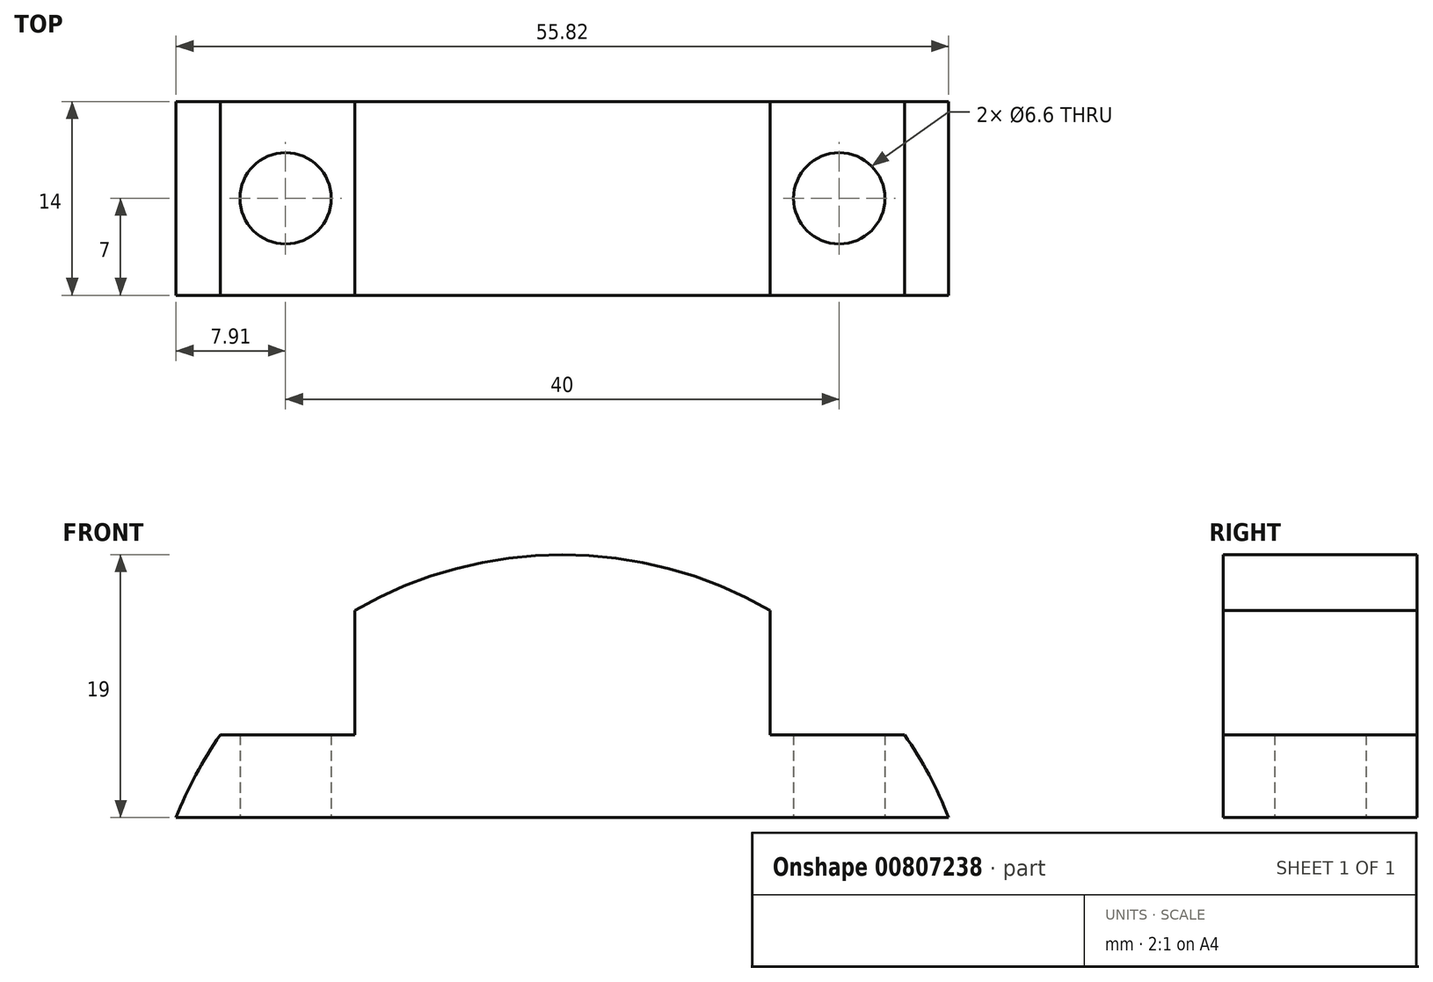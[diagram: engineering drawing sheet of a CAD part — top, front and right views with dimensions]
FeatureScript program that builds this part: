
annotation { "Feature Type Name" : "Feature", "Feature Type Description" : "" }
export const myFeature = defineFeature(function(context is Context, id is Id, definition is map)
    precondition{}
    {
        {
            var Q0;
            Q0=qCreatedBy(makeId("Front.planeOp"),FACE);
            var sketch = newSketch(context, id + "F0", { "sketchPlane" : qUnion([Q0])});
            skArc(sketch, "E0", {"start": v(27.91, 11) * mm, "mid": v(26.48, 14.1) * mm, "end": v(24.72, 17) * mm});
            skLineSegment(sketch, "E1", {"start": v(-27.91, 11) * mm, "end": v(27.91, 11) * mm});
            skLineSegment(sketch, "E2", {"start": v(0, 0) * mm, "end": v(0, -11.85) * mm, "construction": true});
            skLineSegment(sketch, "E3", {"start": v(-24.72, 17) * mm, "end": v(-15, 17) * mm});
            skLineSegment(sketch, "E4", {"start": v(15, 17) * mm, "end": v(15, 25.98) * mm});
            skLineSegment(sketch, "E5.MirrorCS", {"start": v(-15, 17) * mm, "end": v(-15, 25.98) * mm});
            skArc(sketch, "E6.trimOffspring", {"start": v(15, 25.98) * mm, "mid": v(0, 30) * mm, "end": v(-15, 25.98) * mm});
            skArc(sketch, "E7.trimOffspring", {"start": v(-24.72, 17) * mm, "mid": v(-26.48, 14.1) * mm, "end": v(-27.91, 11) * mm});
            skLineSegment(sketch, "E8.trimOffspring", {"start": v(15, 17) * mm, "end": v(24.72, 17) * mm});
            skSolve(sketch);
        }
        {
            var Q0;
            Q0 = qSketchRegion(id + "F0", true);
            extrude(context, id + "F1", {"entities" : qUnion([Q0]), "depth" : 14 * mm, "offsetDistance" : 25 * mm, "symmetric" : true});
        }
        {
            var Q0;
            Q0=makeQuery(id+"F1.opExtrude","SWEPT_FACE",FACE,{"disambiguationData":[OSD([sQuery(id+"F0.wireOp",EDGE,"E1")])]});
            var sketch = newSketch(context, id + "F2", { "sketchPlane" : qUnion([Q0])});
            skLineSegment(sketch, "E9", {"start": v(-20, 0) * mm, "end": v(20, 0) * mm, "construction": true});
            skPoint(sketch, "E10", {"position": v(-20, 0) * mm});
            skPoint(sketch, "E11", {"position": v(20, 0) * mm});
            skSolve(sketch);
        }
        {
            var Q0;
            Q0=sQuery(id+"F2.wireOp",VERTEX,"E10");
            var Q1;
            Q1=sQuery(id+"F2.wireOp",VERTEX,"E11");
            var Q2;
            Q2=makeQuery(id+"F1.opExtrude","SWEPT_BODY",BODY,{"disambiguationData":[OSD([sQuery(id+"F0.wireOp",EDGE,"E0"),sQuery(id+"F0.wireOp",EDGE,"E1"),sQuery(id+"F0.wireOp",EDGE,"E3"),sQuery(id+"F0.wireOp",EDGE,"E4"),sQuery(id+"F0.wireOp",EDGE,"E5.MirrorCS"),sQuery(id+"F0.wireOp",EDGE,"E6.trimOffspring"),sQuery(id+"F0.wireOp",EDGE,"E7.trimOffspring"),sQuery(id+"F0.wireOp",EDGE,"E8.trimOffspring")])]});
            hole(context, id + "F3", {"style" : HoleStyle.SIMPLE, "endStyle" : HoleEndStyle.THROUGH, "holeDiameter" : 6.6 * mm, "majorDiameter" : 5 * mm, "tappedDepth" : 12 * mm, "tapClearance" : 3, "startFromSketch" : true, "locations" : qUnion([Q0, Q1]), "scope" : qUnion([Q2])});
        }
    });
